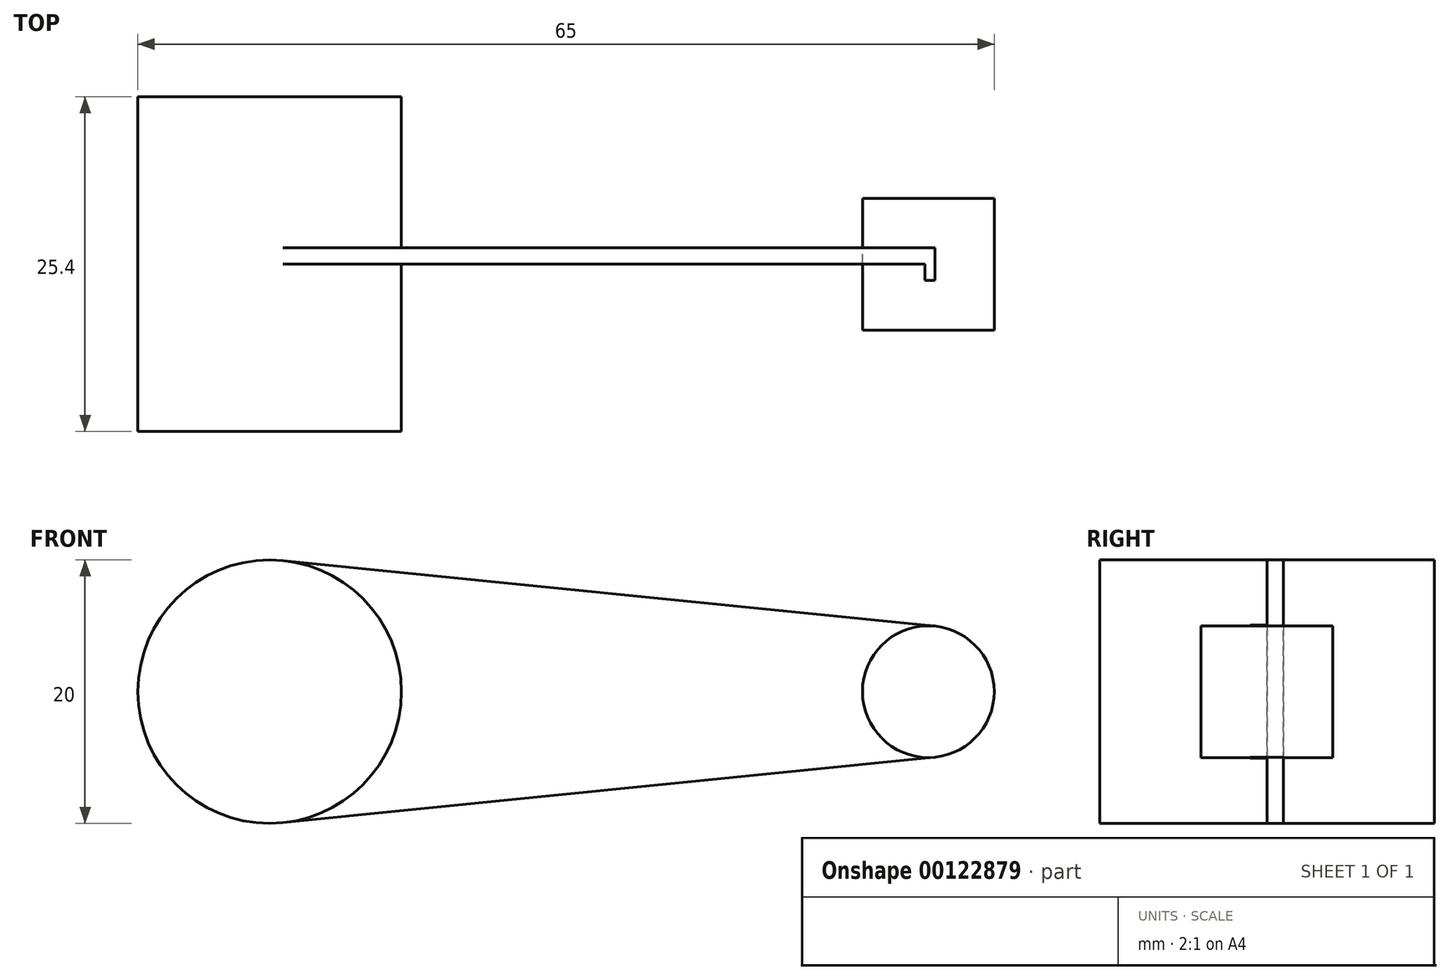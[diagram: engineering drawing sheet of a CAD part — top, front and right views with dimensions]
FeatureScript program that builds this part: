
annotation { "Feature Type Name" : "Feature", "Feature Type Description" : "" }
export const myFeature = defineFeature(function(context is Context, id is Id, definition is map)
    precondition{}
    {
        {
            var Q0;
            Q0=qCreatedBy(makeId("Front.planeOp"),FACE);
            var sketch = newSketch(context, id + "F0", { "sketchPlane" : qUnion([Q0])});
            skCircle(sketch, "E0", {"center": v(0, 0) * mm, "radius": 5 * mm});
            skCircle(sketch, "E1", {"center": v(-50, 0) * mm, "radius": 10 * mm});
            skLineSegment(sketch, "E2", {"start": v(-49, 9.95) * mm, "end": v(0.5, 4.97) * mm});
            skLineSegment(sketch, "E3", {"start": v(-49, -9.95) * mm, "end": v(0.5, -4.97) * mm});
            skSolve(sketch);
        }
        {
            var Q0;
            {var subQ0=sQuery(id+"F0.wireOp",EDGE,"E1");var subQ1=makeQuery(id+"F0.imprint","INTERSECT",VERTEX,{"derivedFrom":[subQ0,sQuery(id+"F0.wireOp",EDGE,"E2")]});Q0=makeQuery(id+"F0.imprint","IMPRINT",FACE,{"disambiguationData":[TD([[makeQuery(id+"F0.imprint","IMPRINT",EDGE,{"disambiguationData":[TD([[subQ1,-1.0]])],"derivedFrom":subQ0}),1.0]])]});}
            extrude(context, id + "F1", {"entities" : qUnion([Q0]), "endBound" : BoundingType.SYMMETRIC, "depth" : 5 * mm, "hasSecondDirection" : true, "secondDirectionOppositeDirection" : true, "secondDirectionDepth" : 25.4 * mm});
        }
        {
            var Q0;
            {var subQ0=sQuery(id+"F0.wireOp",EDGE,"E0");var subQ1=makeQuery(id+"F0.imprint","INTERSECT",VERTEX,{"derivedFrom":[subQ0,sQuery(id+"F0.wireOp",EDGE,"E2")]});Q0=makeQuery(id+"F0.imprint","IMPRINT",FACE,{"disambiguationData":[TD([[makeQuery(id+"F0.imprint","IMPRINT",EDGE,{"disambiguationData":[TD([[subQ1,-1.0]])],"derivedFrom":subQ0}),1.0]])]});}
            var Q1;
            Q1=sQuery(id+"F0.wireOp",EDGE,"E0");
            extrude(context, id + "F2", {"entities" : qUnion([Q0]), "surfaceEntities" : qUnion([Q1]), "endBound" : BoundingType.SYMMETRIC, "depth" : 10 * mm});
        }
        {
            var Q0;
            {var subQ0=sQuery(id+"F0.wireOp",EDGE,"E2");Q0=makeQuery(id+"F0.imprint","IMPRINT",FACE,{"disambiguationData":[TD([[makeQuery(id+"F0.imprint","IMPRINT",EDGE,{"derivedFrom":subQ0}),-1.0]])]});}
            extrude(context, id + "F3", {"entities" : qUnion([Q0]), "endBound" : BoundingType.SYMMETRIC, "depth" : 2.5 * mm});
        }
        {
            var Q0;
            Q0=sQuery(id+"F0.wireOp",VERTEX,"E1.center");
            var Q1;
            Q1=sQuery(id+"F0.wireOp",VERTEX,"E0.center");
            var Q2;
            Q2=makeQuery(id+"F1.opExtrude","SWEPT_BODY",BODY,{"disambiguationData":[OSD([sQuery(id+"F0.wireOp",EDGE,"E1")])]});
            hole(context, id + "F4", {"style" : HoleStyle.SIMPLE, "endStyle" : HoleEndStyle.BLIND, "holeDiameter" : 100 * mm, "holeDepth" : 12.7 * mm, "locations" : qUnion([Q0, Q1]), "scope" : qUnion([Q2])});
        }
        {
            var Q0;
            Q0=sQuery(id+"F0.wireOp",VERTEX,"E1.center");
            var Q1;
            Q1=makeQuery(id+"F1.opExtrude","SWEPT_BODY",BODY,{"disambiguationData":[OSD([sQuery(id+"F0.wireOp",EDGE,"E1")])]});
            var Q2;
            Q2=makeQuery(id+"F3.opExtrude","SWEPT_BODY",BODY,{"disambiguationData":[OSD([sQuery(id+"F0.wireOp",EDGE,"E0"),sQuery(id+"F0.wireOp",EDGE,"E1"),sQuery(id+"F0.wireOp",EDGE,"E2"),sQuery(id+"F0.wireOp",EDGE,"E3")])]});
            hole(context, id + "F5", {"style" : HoleStyle.SIMPLE, "endStyle" : HoleEndStyle.BLIND, "oppositeDirection" : true, "holeDiameter" : 100 * mm, "holeDepth" : 12.7 * mm, "locations" : qUnion([Q0]), "scope" : qUnion([Q1, Q2])});
        }
        {
            var Q0;
            {var subQ0=sQuery(id+"F0.wireOp",EDGE,"E1");var subQ1=makeQuery(id+"F0.imprint","INTERSECT",VERTEX,{"derivedFrom":[subQ0,sQuery(id+"F0.wireOp",EDGE,"E2")]});Q0=makeQuery(id+"F0.imprint","IMPRINT",FACE,{"disambiguationData":[TD([[makeQuery(id+"F0.imprint","IMPRINT",EDGE,{"disambiguationData":[TD([[subQ1,-1.0]])],"derivedFrom":subQ0}),1.0]])]});}
            extrude(context, id + "F6", {"entities" : qUnion([Q0]), "operationType" : NewBodyOperationType.ADD, "endBound" : BoundingType.SYMMETRIC, "depth" : 25.4 * mm});
        }
    });
